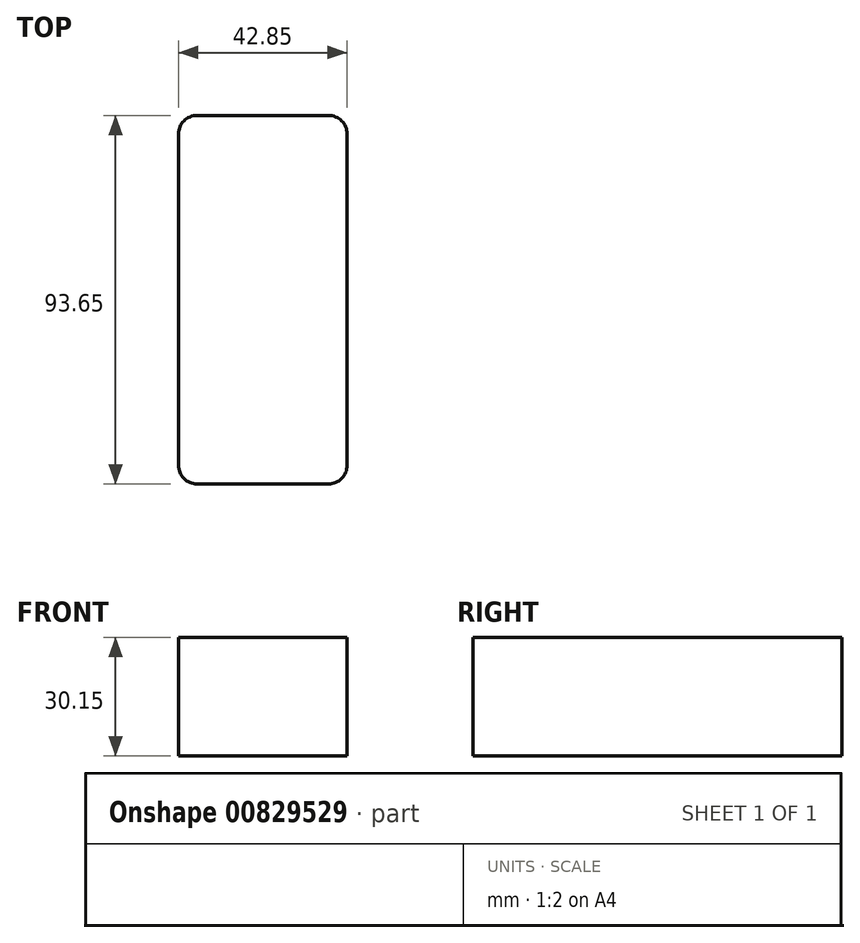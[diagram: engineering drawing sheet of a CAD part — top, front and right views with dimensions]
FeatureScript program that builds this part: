
annotation { "Feature Type Name" : "Feature", "Feature Type Description" : "" }
export const myFeature = defineFeature(function(context is Context, id is Id, definition is map)
    precondition{}
    {
        {
            var Q0;
            Q0=qCreatedBy(makeId("Top.planeOp"),FACE);
            var sketch = newSketch(context, id + "F0", { "sketchPlane" : qUnion([Q0])});
            skLineSegment(sketch, "E0.bottom", {"start": v(4.76, 0) * mm, "end": v(38.09, 0) * mm});
            skLineSegment(sketch, "E0.top", {"start": v(4.76, 93.65) * mm, "end": v(38.09, 93.65) * mm});
            skLineSegment(sketch, "E0.left", {"start": v(0, 4.76) * mm, "end": v(0, 88.89) * mm});
            skLineSegment(sketch, "E0.right", {"start": v(42.85, 4.76) * mm, "end": v(42.85, 88.89) * mm});
            skPoint(sketch, "E1.visualSharp", {"position": v(0, 93.65) * mm});
            skArc(sketch, "E1.filletArc", {"start": v(4.76, 93.65) * mm, "mid": v(1.4, 92.25) * mm, "end": v(0, 88.89) * mm});
            skPoint(sketch, "E2.visualSharp", {"position": v(42.85, 93.65) * mm});
            skArc(sketch, "E2.filletArc", {"start": v(42.85, 88.89) * mm, "mid": v(41.45, 92.25) * mm, "end": v(38.09, 93.65) * mm});
            skPoint(sketch, "E3.visualSharp", {"position": v(42.85, 0) * mm});
            skArc(sketch, "E3.filletArc", {"start": v(38.09, 0) * mm, "mid": v(41.45, 1.4) * mm, "end": v(42.85, 4.76) * mm});
            skPoint(sketch, "E4.visualSharp", {"position": v(0, 0) * mm});
            skArc(sketch, "E4.filletArc", {"start": v(0, 4.76) * mm, "mid": v(1.4, 1.4) * mm, "end": v(4.76, 0) * mm});
            skSolve(sketch);
        }
        {
            var Q0;
            Q0=makeQuery(id+"F0.imprint","IMPRINT",FACE,{"disambiguationData":[TD([[makeQuery(id+"F0.imprint","IMPRINT",EDGE,{"derivedFrom":sQuery(id+"F0.wireOp",EDGE,"E0.bottom")}),1.0]])]});
            extrude(context, id + "F1", {"entities" : qUnion([Q0]), "depth" : 30.15 * mm, "offsetDistance" : 25.4 * mm});
        }
    });
